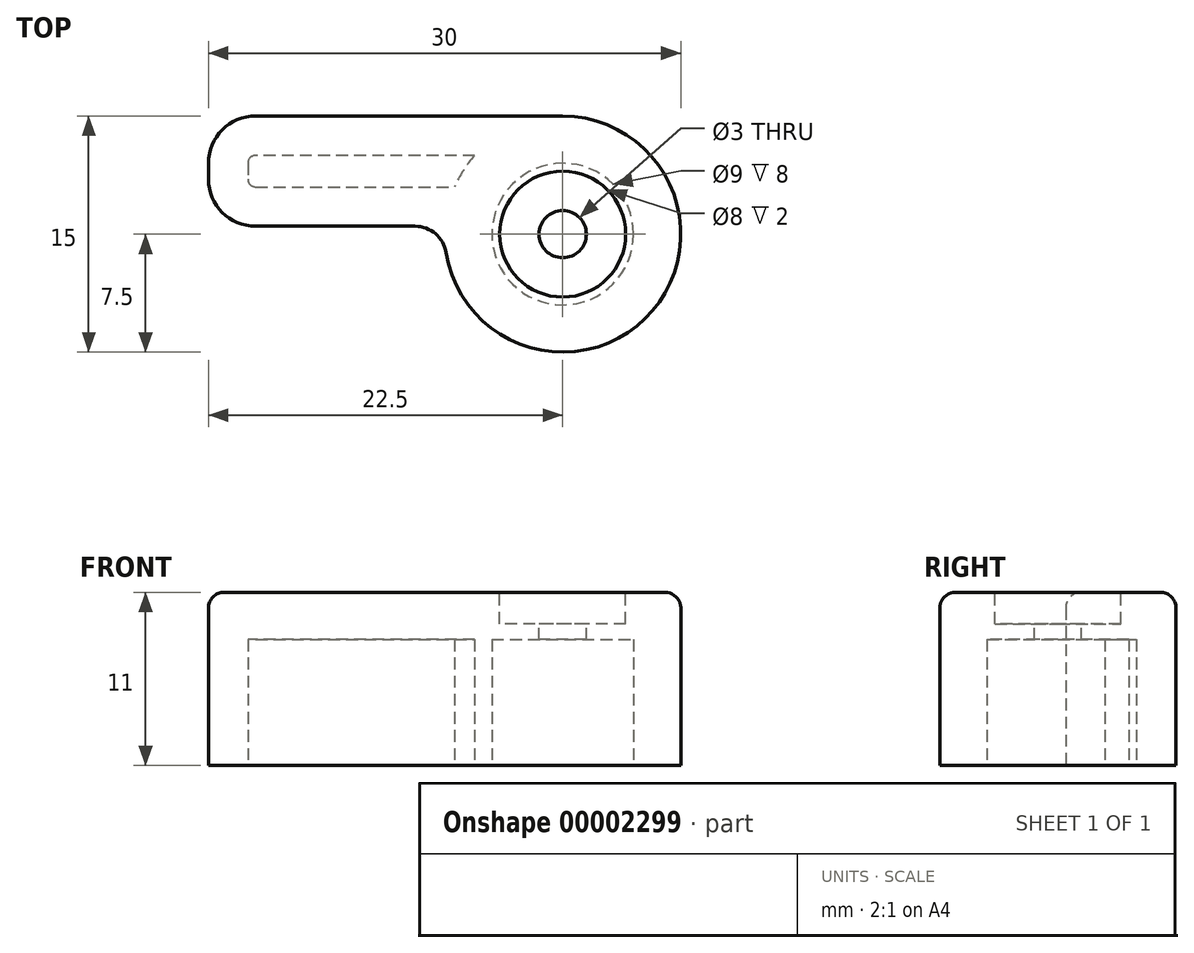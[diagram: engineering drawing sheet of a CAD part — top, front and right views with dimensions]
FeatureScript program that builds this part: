
annotation { "Feature Type Name" : "Feature", "Feature Type Description" : "" }
export const myFeature = defineFeature(function(context is Context, id is Id, definition is map)
    precondition{}
    {
        {
            var Q0;
            Q0=qCreatedBy(makeId("Top.planeOp"),FACE);
            var sketch = newSketch(context, id + "F0", { "sketchPlane" : qUnion([Q0])});
            skArc(sketch, "E0", {"start": v(-7.4, -1.18) * mm, "mid": v(5.7, -4.87) * mm, "end": v(0, 7.5) * mm});
            skCircle(sketch, "E1", {"center": v(0, 0) * mm, "radius": 4.5 * mm});
            skLineSegment(sketch, "E2", {"start": v(0, 7.5) * mm, "end": v(-19.5, 7.5) * mm});
            skLineSegment(sketch, "E3", {"start": v(-22.5, 4.5) * mm, "end": v(-22.5, 3.5) * mm});
            skLineSegment(sketch, "E4", {"start": v(-19.5, 0.5) * mm, "end": v(-9.38, 0.5) * mm});
            skPoint(sketch, "E5.visualSharp", {"position": v(-22.5, 7.5) * mm});
            skArc(sketch, "E5.filletArc", {"start": v(-19.5, 7.5) * mm, "mid": v(-21.62, 6.62) * mm, "end": v(-22.5, 4.5) * mm});
            skPoint(sketch, "E6.visualSharp", {"position": v(-22.5, 0.5) * mm});
            skArc(sketch, "E6.filletArc", {"start": v(-22.5, 3.5) * mm, "mid": v(-21.62, 1.38) * mm, "end": v(-19.5, 0.5) * mm});
            skPoint(sketch, "E7.visualSharp", {"position": v(-7.48, 0.5) * mm});
            skArc(sketch, "E7.filletArc", {"start": v(-7.4, -1.18) * mm, "mid": v(-8.08, 0.02) * mm, "end": v(-9.38, 0.5) * mm});
            skSolve(sketch);
        }
        {
            var Q0;
            Q0=makeQuery(id+"F0.imprint","IMPRINT",FACE,{"disambiguationData":[TD([[makeQuery(id+"F0.imprint","IMPRINT",EDGE,{"derivedFrom":sQuery(id+"F0.wireOp",EDGE,"E0")}),1.0]])]});
            var Q1;
            Q1=makeQuery(id+"F0.imprint","IMPRINT",FACE,{"disambiguationData":[TD([[makeQuery(id+"F0.imprint","IMPRINT",EDGE,{"derivedFrom":sQuery(id+"F0.wireOp",EDGE,"E1")}),1.0]])]});
            extrude(context, id + "F1", {"entities" : qUnion([Q0, Q1]), "depth" : 11 * mm});
        }
        {
            var Q0;
            Q0=makeQuery(id+"F1.opExtrude","CAP_FACE",FACE,{"disambiguationData":[OSD([sQuery(id+"F0.wireOp",EDGE,"E0"),sQuery(id+"F0.wireOp",EDGE,"E2"),sQuery(id+"F0.wireOp",EDGE,"E3"),sQuery(id+"F0.wireOp",EDGE,"E4"),sQuery(id+"F0.wireOp",EDGE,"E5.filletArc"),sQuery(id+"F0.wireOp",EDGE,"E6.filletArc")])],"isStart":true});
            var sketch = newSketch(context, id + "F2", { "sketchPlane" : qUnion([Q0])});
            skPoint(sketch, "E8.0", {"position": v(0, 0) * mm});
            skCircle(sketch, "E9", {"center": v(0, 0) * mm, "radius": 4.5 * mm});
            skCircle(sketch, "E10", {"center": v(0, 0) * mm, "radius": 7.5 * mm});
            skLineSegment(sketch, "E11.0", {"start": v(-19.5, -0.5) * mm, "end": v(-9.38, -0.5) * mm});
            skArc(sketch, "E12.0", {"start": v(-22.5, -3.5) * mm, "mid": v(-21.62, -1.38) * mm, "end": v(-19.5, -0.5) * mm});
            skLineSegment(sketch, "E13.0", {"start": v(0, -7.5) * mm, "end": v(-19.5, -7.5) * mm});
            skArc(sketch, "E14.0", {"start": v(-19.5, -7.5) * mm, "mid": v(-21.62, -6.62) * mm, "end": v(-22.5, -4.5) * mm});
            skLineSegment(sketch, "E15.0", {"start": v(-22.5, -4.5) * mm, "end": v(-22.5, -3.5) * mm});
            skLineSegment(sketch, "E16.0", {"start": v(-19.5, -3) * mm, "end": v(-7.48, -3) * mm});
            skArc(sketch, "E16.1", {"start": v(-20, -3.5) * mm, "mid": v(-19.85, -3.15) * mm, "end": v(-19.5, -3) * mm});
            skLineSegment(sketch, "E16.2", {"start": v(-20, -4.5) * mm, "end": v(-20, -3.5) * mm});
            skArc(sketch, "E16.3", {"start": v(-19.5, -5) * mm, "mid": v(-19.85, -4.85) * mm, "end": v(-20, -4.5) * mm});
            skLineSegment(sketch, "E16.4", {"start": v(-5.6, -5) * mm, "end": v(-19.5, -5) * mm});
            skLineSegment(sketch, "E17", {"start": v(-7.48, -3) * mm, "end": v(-6.87, -3) * mm});
            skSolve(sketch);
        }
        {
            var Q0;
            Q0=makeQuery(id+"F2.imprint","IMPRINT",FACE,{"disambiguationData":[TD([[makeQuery(id+"F2.imprint","IMPRINT",EDGE,{"derivedFrom":sQuery(id+"F2.wireOp",EDGE,"E9")}),1.0]])]});
            var Q1;
            Q1=makeQuery(id+"F2.imprint","IMPRINT",FACE,{"disambiguationData":[TD([[makeQuery(id+"F2.imprint","IMPRINT",EDGE,{"derivedFrom":sQuery(id+"F2.wireOp",EDGE,"E16.0")}),-1.0]])]});
            extrude(context, id + "F3", {"entities" : qUnion([Q0, Q1]), "operationType" : NewBodyOperationType.REMOVE, "oppositeDirection" : true, "depth" : 8 * mm});
        }
        {
            var Q0;
            Q0=makeQuery(id+"F1.opExtrude","CAP_FACE",FACE,{"disambiguationData":[OSD([sQuery(id+"F0.wireOp",EDGE,"E0"),sQuery(id+"F0.wireOp",EDGE,"E2"),sQuery(id+"F0.wireOp",EDGE,"E3"),sQuery(id+"F0.wireOp",EDGE,"E4"),sQuery(id+"F0.wireOp",EDGE,"E5.filletArc"),sQuery(id+"F0.wireOp",EDGE,"E6.filletArc")])],"isStart":false});
            var sketch = newSketch(context, id + "F4", { "sketchPlane" : qUnion([Q0])});
            skPoint(sketch, "E18.0", {"position": v(0, 0) * mm});
            skCircle(sketch, "E19", {"center": v(0, 0) * mm, "radius": 1.5 * mm});
            skCircle(sketch, "E20", {"center": v(0, 0) * mm, "radius": 4.87 * mm});
            skSolve(sketch);
        }
        {
            var Q0;
            Q0=makeQuery(id+"F4.imprint","IMPRINT",FACE,{"disambiguationData":[TD([[makeQuery(id+"F4.imprint","IMPRINT",EDGE,{"derivedFrom":sQuery(id+"F4.wireOp",EDGE,"E19")}),1.0]])]});
            extrude(context, id + "F5", {"entities" : qUnion([Q0]), "operationType" : NewBodyOperationType.REMOVE, "endBound" : BoundingType.THROUGH_ALL, "oppositeDirection" : true, "depth" : 25 * mm});
        }
        {
            var Q0;
            Q0=makeQuery(id+"F1.opExtrude","CAP_FACE",FACE,{"disambiguationData":[OSD([sQuery(id+"F0.wireOp",EDGE,"E0"),sQuery(id+"F0.wireOp",EDGE,"E2"),sQuery(id+"F0.wireOp",EDGE,"E3"),sQuery(id+"F0.wireOp",EDGE,"E4"),sQuery(id+"F0.wireOp",EDGE,"E5.filletArc"),sQuery(id+"F0.wireOp",EDGE,"E6.filletArc")])],"isStart":false});
            var sketch = newSketch(context, id + "F6", { "sketchPlane" : qUnion([Q0])});
            skCircle(sketch, "E21", {"center": v(0, 0) * mm, "radius": 4 * mm});
            skSolve(sketch);
        }
        {
            var Q0;
            Q0=makeQuery(id+"F6.imprint","IMPRINT",FACE,{"disambiguationData":[TD([[makeQuery(id+"F6.imprint","IMPRINT",EDGE,{"derivedFrom":sQuery(id+"F6.wireOp",EDGE,"E21")}),1.0]])]});
            extrude(context, id + "F7", {"entities" : qUnion([Q0]), "operationType" : NewBodyOperationType.REMOVE, "oppositeDirection" : true, "depth" : 2 * mm});
        }
        {
            var Q0;
            Q0=makeQuery(id+"F1.opExtrude","CAP_EDGE",EDGE,{"disambiguationData":[OSD([sQuery(id+"F0.wireOp",EDGE,"E2")])],"isStart":false});
            fillet(context, id + "F8", {"entities" : qUnion([Q0]), "radius" : 1 * mm, "tangentPropagation" : true, "allowEdgeOverflow" : false});
        }
    });
